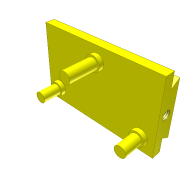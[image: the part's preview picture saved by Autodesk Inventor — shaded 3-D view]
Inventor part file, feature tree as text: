
AUTODESK INVENTOR PART (.ipt)
format: ipt  version: unknown  size: 231,424 bytes
history: native  units: in
note: dims shown in document units (in); Inventor stores cm internally (conversion verified against a paired STEP export)
features: sketch x6, extrude x6, plane x1, thread x1
ambient origin geometry x8: Origin, YZ Plane, XZ Plane, XY Plane, X Axis, Y Axis, Z Axis, Center Point
feature tree (14):
  sketch  "Sketch9"  dims[d49=3.937in d50=15.748in]
  plane  "Work Plane8"
  extrude  "Extrusion5"  Depth=15.748in
  extrude  "Extrusion6"  Depth=1.9685in
  extrude  "Extrusion7"  Depth=1.9685in
  extrude  "Extrusion8"  Depth=7.874in
  extrude  "Extrusion9"  Depth=0.4724in
  thread  "Thread1"  [1 undecoded]
  extrude  "Extrusion10"  Depth=0.1969in TaperAngle=0.0deg
  sketch  "Sketch17"  dims[d58=0.9843in d59=1.9685in]
  sketch  "Sketch18"  dims[d60=1.9685in d61=1.9685in]
  sketch  "Sketch19"  dims[d62=1.9685in d64=7.874in]
  sketch  "Sketch20"  dims[d65=7.874in d71=0.4724in d72=0.7874in d73=0.0in]
  sketch  "Sketch21"  dims[d74=0.0787in d75=0.1969in d76=0.0in d77=0.5906in d78=0.5906in d79=0.5906in d80=0.5906in d81=0.3937in d82=0.0in d83=0.3937in d84=60.0deg d85=60.0deg d86=1.1811in d87=2.3622in d88=0.3937in d89=0.0in d90=0.3937in d91=0.3937in d92=0.0in d93=0.3937in d94=0.0in d95=0.3937in d96=0.0in]
note: 1 required parameter value undecoded (feature->parameter linkage not recoverable at this tier; creation-order binding heuristic only, values carry confidence <= 0.55)
